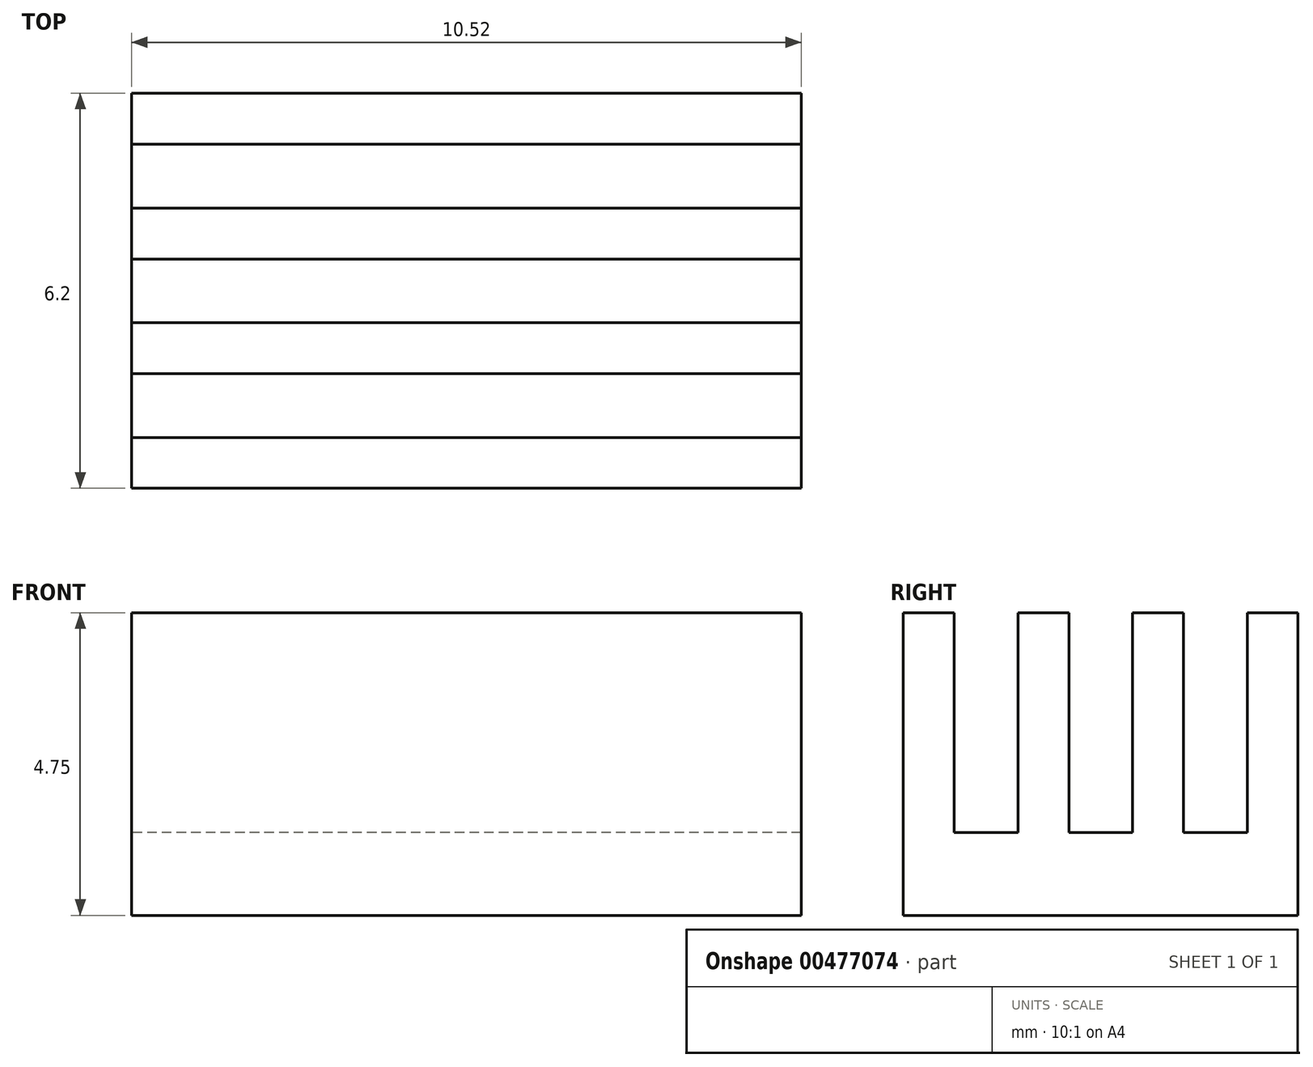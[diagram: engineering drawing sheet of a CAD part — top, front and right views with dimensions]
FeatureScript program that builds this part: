
annotation { "Feature Type Name" : "Feature", "Feature Type Description" : "" }
export const myFeature = defineFeature(function(context is Context, id is Id, definition is map)
    precondition{}
    {
        {
            var Q0;
            Q0=qCreatedBy(makeId("Top.planeOp"),FACE);
            var sketch = newSketch(context, id + "F0", { "sketchPlane" : qUnion([Q0])});
            skLineSegment(sketch, "E0.bottom", {"start": v(5.26, 2.2) * mm, "end": v(-5.26, 2.2) * mm});
            skLineSegment(sketch, "E0.top", {"start": v(5.26, -2.2) * mm, "end": v(-5.26, -2.2) * mm});
            skLineSegment(sketch, "E0.left", {"start": v(5.26, 2.2) * mm, "end": v(5.26, -2.2) * mm});
            skLineSegment(sketch, "E0.right", {"start": v(-5.26, 2.2) * mm, "end": v(-5.26, -2.2) * mm});
            skPoint(sketch, "E0.middle", {"position": v(0, 0) * mm});
            skLineSegment(sketch, "E1", {"start": v(-5.26, 1.4) * mm, "end": v(5.26, 1.4) * mm});
            skLineSegment(sketch, "E2", {"start": v(-5.26, 0.4) * mm, "end": v(5.26, 0.4) * mm});
            skLineSegment(sketch, "E3", {"start": v(5.26, 0.4) * mm, "end": v(5.26, -0.4) * mm});
            skLineSegment(sketch, "E4", {"start": v(5.26, -0.4) * mm, "end": v(-5.26, -0.4) * mm});
            skLineSegment(sketch, "E5", {"start": v(-5.26, -0.4) * mm, "end": v(-5.26, -1.4) * mm});
            skLineSegment(sketch, "E6", {"start": v(-5.26, -1.4) * mm, "end": v(5.26, -1.4) * mm});
            skLineSegment(sketch, "E7", {"start": v(-5.26, -2.2) * mm, "end": v(-5.26, -3.2) * mm});
            skLineSegment(sketch, "E8", {"start": v(-5.26, -3.2) * mm, "end": v(5.26, -3.2) * mm});
            skLineSegment(sketch, "E9", {"start": v(5.26, -3.2) * mm, "end": v(5.26, -2.2) * mm});
            skLineSegment(sketch, "E10", {"start": v(-5.26, -3.2) * mm, "end": v(-5.26, -4) * mm});
            skLineSegment(sketch, "E11", {"start": v(-5.26, -4) * mm, "end": v(5.26, -4) * mm});
            skLineSegment(sketch, "E12", {"start": v(5.26, -4) * mm, "end": v(5.26, -3.2) * mm});
            skSolve(sketch);
        }
        {
            var Q0;
            Q0 = qSketchRegion(id + "F0", true);
            extrude(context, id + "F1", {"entities" : qUnion([Q0]), "depth" : 1.3 * mm});
        }
        {
            var Q0;
            {var subQ0=sQuery(id+"F0.wireOp",EDGE,"E0.bottom");Q0=makeQuery(id+"F0.imprint","IMPRINT",FACE,{"disambiguationData":[TD([[makeQuery(id+"F0.imprint","IMPRINT",EDGE,{"derivedFrom":subQ0}),1.0]])]});}
            var Q1;
            {var subQ0=sQuery(id+"F0.wireOp",EDGE,"E2");Q1=makeQuery(id+"F0.imprint","IMPRINT",FACE,{"disambiguationData":[TD([[makeQuery(id+"F0.imprint","IMPRINT",EDGE,{"derivedFrom":subQ0}),-1.0]])]});}
            var Q2;
            {var subQ0=sQuery(id+"F0.wireOp",EDGE,"E0.top");Q2=makeQuery(id+"F0.imprint","IMPRINT",FACE,{"disambiguationData":[TD([[makeQuery(id+"F0.imprint","IMPRINT",EDGE,{"derivedFrom":subQ0}),-1.0]])]});}
            var Q3;
            Q3=makeQuery(id+"F0.imprint","IMPRINT",FACE,{"disambiguationData":[TD([[makeQuery(id+"F0.imprint","IMPRINT",EDGE,{"derivedFrom":sQuery(id+"F0.wireOp",EDGE,"E8")}),-1.0]])]});
            extrude(context, id + "F2", {"entities" : qUnion([Q0, Q1, Q2, Q3]), "operationType" : NewBodyOperationType.ADD, "depth" : 4.75 * mm});
        }
    });
